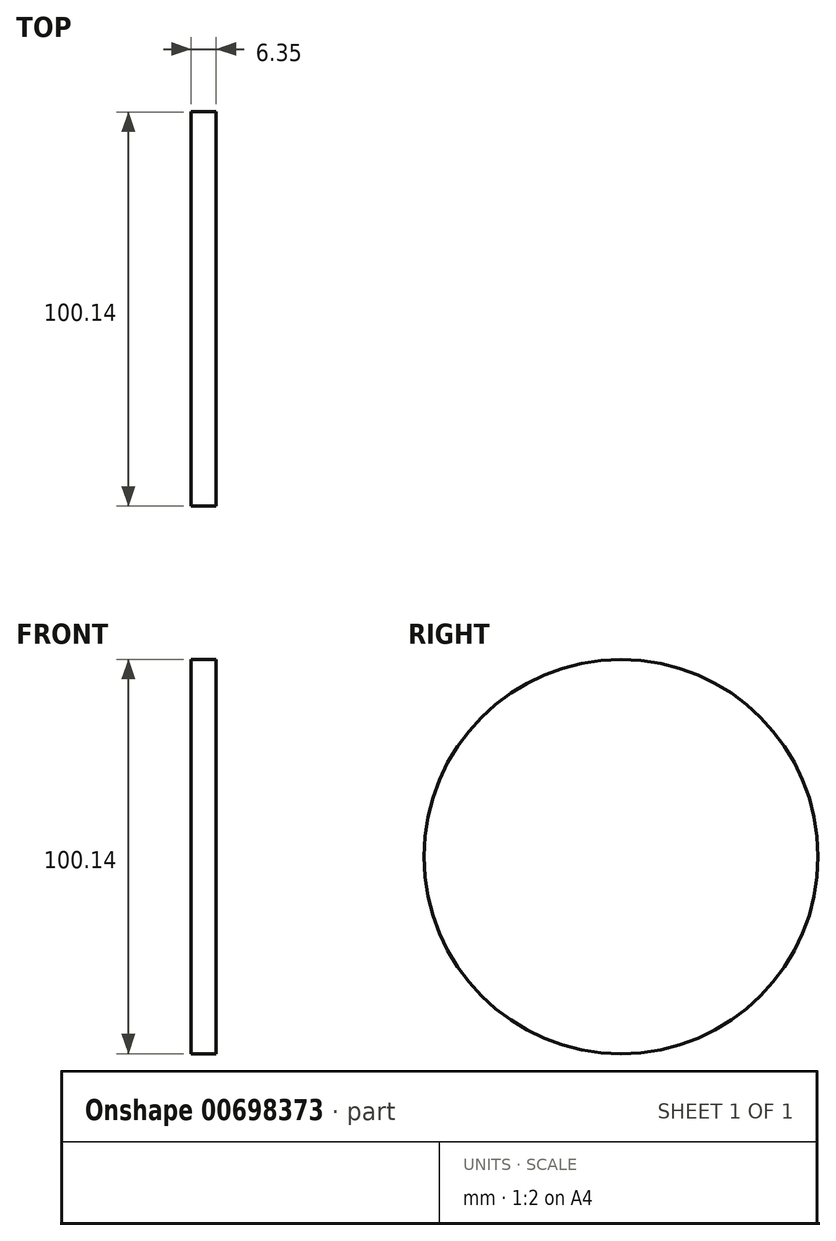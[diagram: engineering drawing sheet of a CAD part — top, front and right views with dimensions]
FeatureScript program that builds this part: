
annotation { "Feature Type Name" : "Feature", "Feature Type Description" : "" }
export const myFeature = defineFeature(function(context is Context, id is Id, definition is map)
    precondition{}
    {
        {
            var Q0;
            Q0=qCreatedBy(makeId("Right.planeOp"),FACE);
            var sketch = newSketch(context, id + "F0", { "sketchPlane" : qUnion([Q0])});
            skCircle(sketch, "E0", {"center": v(0, 0) * mm, "radius": 50.07 * mm});
            skSolve(sketch);
        }
        {
            var Q0;
            Q0 = qSketchRegion(id + "F0", true);
            extrude(context, id + "F1", {"entities" : qUnion([Q0]), "depth" : 6.35 * mm, "offsetDistance" : 25.4 * mm});
        }
    });
